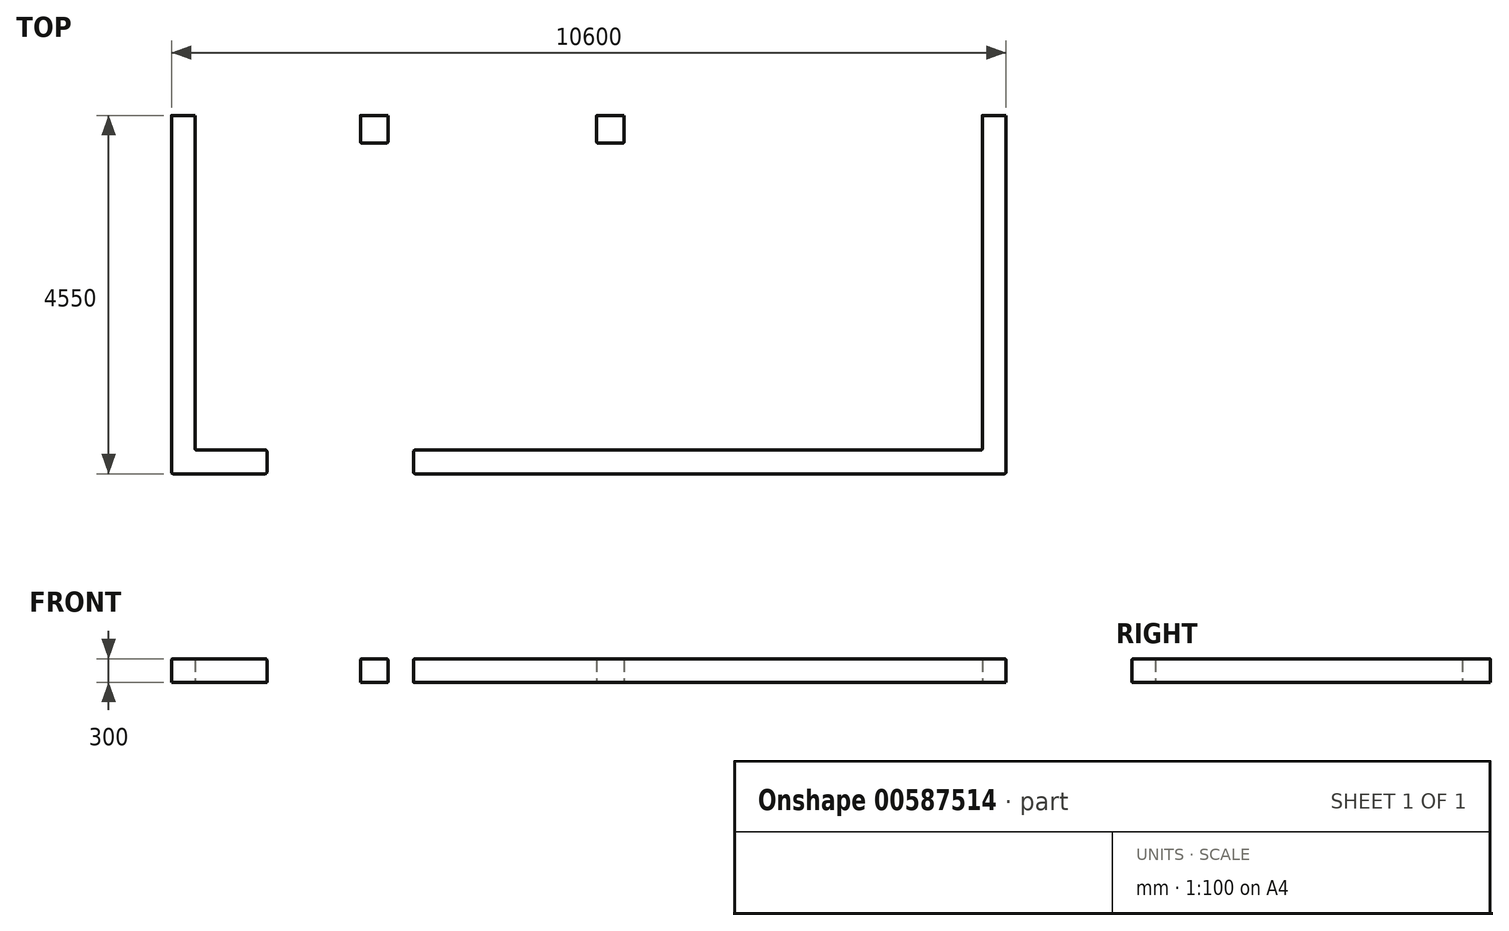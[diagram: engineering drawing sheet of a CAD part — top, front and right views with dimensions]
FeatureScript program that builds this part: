
annotation { "Feature Type Name" : "Feature", "Feature Type Description" : "" }
export const myFeature = defineFeature(function(context is Context, id is Id, definition is map)
    precondition{}
    {
        {
            var Q0;
            Q0=qCreatedBy(makeId("Top.planeOp"),FACE);
            var sketch = newSketch(context, id + "F0", { "sketchPlane" : qUnion([Q0])});
            skLineSegment(sketch, "E0.bottom", {"start": v(0, 0) * mm, "end": v(1211.59, 0) * mm});
            skLineSegment(sketch, "E0.top", {"start": v(0, 4550) * mm, "end": v(300, 4550) * mm});
            skLineSegment(sketch, "E0.left", {"start": v(0, 0) * mm, "end": v(0, 4550) * mm});
            skLineSegment(sketch, "E0.right", {"start": v(10600, 0) * mm, "end": v(10600, 4550) * mm});
            skLineSegment(sketch, "E1.1", {"start": v(300, 300) * mm, "end": v(300, 4550) * mm});
            skLineSegment(sketch, "E1.2", {"start": v(300, 300) * mm, "end": v(1211.59, 300) * mm});
            skLineSegment(sketch, "E1.3", {"start": v(10300, 300) * mm, "end": v(10300, 4550) * mm});
            skLineSegment(sketch, "E2.left", {"start": v(1211.59, 300) * mm, "end": v(1211.59, 0) * mm});
            skLineSegment(sketch, "E2.right", {"start": v(3074.35, 300) * mm, "end": v(3074.35, 0) * mm});
            skLineSegment(sketch, "E3.trimOffspring", {"start": v(3074.35, 300) * mm, "end": v(10300, 300) * mm});
            skLineSegment(sketch, "E4.trimOffspring", {"start": v(3074.35, 0) * mm, "end": v(10600, 0) * mm});
            skLineSegment(sketch, "E5.trimOffspring", {"start": v(10300, 4550) * mm, "end": v(10600, 4550) * mm});
            skLineSegment(sketch, "E6.bottom", {"start": v(2400, 4550) * mm, "end": v(2750, 4550) * mm});
            skLineSegment(sketch, "E6.top", {"start": v(2400, 4200) * mm, "end": v(2750, 4200) * mm});
            skLineSegment(sketch, "E6.left", {"start": v(2400, 4550) * mm, "end": v(2400, 4200) * mm});
            skLineSegment(sketch, "E6.right", {"start": v(2750, 4550) * mm, "end": v(2750, 4200) * mm});
            skLineSegment(sketch, "E7.bottom", {"start": v(5400, 4550) * mm, "end": v(5750, 4550) * mm});
            skLineSegment(sketch, "E7.top", {"start": v(5400, 4200) * mm, "end": v(5750, 4200) * mm});
            skLineSegment(sketch, "E7.left", {"start": v(5400, 4550) * mm, "end": v(5400, 4200) * mm});
            skLineSegment(sketch, "E7.right", {"start": v(5750, 4550) * mm, "end": v(5750, 4200) * mm});
            skSolve(sketch);
        }
        {
            var Q0;
            Q0 = qSketchRegion(id + "F0", true);
            extrude(context, id + "F1", {"entities" : qUnion([Q0]), "depth" : 300 * mm, "offsetDistance" : 25 * mm});
        }
        {
            var Q0;
            Q0=makeQuery(id+"F1.opExtrude","CAP_EDGE",EDGE,{"disambiguationData":[OSD([sQuery(id+"F0.wireOp",EDGE,"E1.1")])],"isStart":false});
            var Q1;
            Q1=makeQuery(id+"F1.opExtrude","CAP_EDGE",EDGE,{"disambiguationData":[OSD([sQuery(id+"F0.wireOp",EDGE,"E0.left")])],"isStart":false});
            var Q2;
            Q2=makeQuery(id+"F1.opExtrude","CAP_EDGE",EDGE,{"disambiguationData":[OSD([sQuery(id+"F0.wireOp",EDGE,"E1.2")])],"isStart":false});
            var Q3;
            Q3=makeQuery(id+"F1.opExtrude","CAP_EDGE",EDGE,{"disambiguationData":[OSD([sQuery(id+"F0.wireOp",EDGE,"E0.bottom")])],"isStart":false});
            var Q4;
            Q4=makeQuery(id+"F1.opExtrude","SWEPT_EDGE",EDGE,{"disambiguationData":[OSD([sQuery(id+"F0.wireOp",EDGE,"E0.bottom"),sQuery(id+"F0.wireOp",EDGE,"E2.left")])]});
            var Q5;
            Q5=makeQuery(id+"F1.opExtrude","CAP_EDGE",EDGE,{"disambiguationData":[OSD([sQuery(id+"F0.wireOp",EDGE,"E2.left")])],"isStart":false});
            var Q6;
            Q6=makeQuery(id+"F1.opExtrude","SWEPT_EDGE",EDGE,{"disambiguationData":[OSD([sQuery(id+"F0.wireOp",EDGE,"E1.2"),sQuery(id+"F0.wireOp",EDGE,"E2.left")])]});
            var Q7;
            Q7=makeQuery(id+"F1.opExtrude","SWEPT_EDGE",EDGE,{"disambiguationData":[OSD([sQuery(id+"F0.wireOp",EDGE,"E2.right"),sQuery(id+"F0.wireOp",EDGE,"E4.trimOffspring")])]});
            var Q8;
            Q8=makeQuery(id+"F1.opExtrude","CAP_EDGE",EDGE,{"disambiguationData":[OSD([sQuery(id+"F0.wireOp",EDGE,"E2.right")])],"isStart":false});
            var Q9;
            Q9=makeQuery(id+"F1.opExtrude","CAP_EDGE",EDGE,{"disambiguationData":[OSD([sQuery(id+"F0.wireOp",EDGE,"E3.trimOffspring")])],"isStart":false});
            var Q10;
            Q10=makeQuery(id+"F1.opExtrude","CAP_EDGE",EDGE,{"disambiguationData":[OSD([sQuery(id+"F0.wireOp",EDGE,"E4.trimOffspring")])],"isStart":false});
            var Q11;
            Q11=makeQuery(id+"F1.opExtrude","SWEPT_EDGE",EDGE,{"disambiguationData":[OSD([sQuery(id+"F0.wireOp",EDGE,"E2.right"),sQuery(id+"F0.wireOp",EDGE,"E3.trimOffspring")])]});
            var Q12;
            Q12=makeQuery(id+"F1.opExtrude","CAP_EDGE",EDGE,{"disambiguationData":[OSD([sQuery(id+"F0.wireOp",EDGE,"E1.3")])],"isStart":false});
            var Q13;
            Q13=makeQuery(id+"F1.opExtrude","CAP_EDGE",EDGE,{"disambiguationData":[OSD([sQuery(id+"F0.wireOp",EDGE,"E0.right")])],"isStart":false});
            var Q14;
            Q14=makeQuery(id+"F1.opExtrude","SWEPT_FACE",FACE,{"disambiguationData":[OSD([sQuery(id+"F0.wireOp",EDGE,"E4.trimOffspring")])]});
            var Q15;
            Q15=makeQuery(id+"F1.opExtrude","SWEPT_EDGE",EDGE,{"disambiguationData":[OSD([sQuery(id+"F0.wireOp",EDGE,"E0.bottom"),sQuery(id+"F0.wireOp",EDGE,"E0.left")])]});
            var Q16;
            Q16=makeQuery(id+"F1.opExtrude","SWEPT_EDGE",EDGE,{"disambiguationData":[OSD([sQuery(id+"F0.wireOp",EDGE,"E1.1"),sQuery(id+"F0.wireOp",EDGE,"E1.2")])]});
            var Q17;
            Q17=makeQuery(id+"F1.opExtrude","SWEPT_EDGE",EDGE,{"disambiguationData":[OSD([sQuery(id+"F0.wireOp",EDGE,"E1.3"),sQuery(id+"F0.wireOp",EDGE,"E3.trimOffspring")])]});
            var Q18;
            Q18=makeQuery(id+"F1.opExtrude","SWEPT_EDGE",EDGE,{"disambiguationData":[OSD([sQuery(id+"F0.wireOp",EDGE,"E6.top"),sQuery(id+"F0.wireOp",EDGE,"E6.left")])]});
            var Q19;
            Q19=makeQuery(id+"F1.opExtrude","CAP_EDGE",EDGE,{"disambiguationData":[OSD([sQuery(id+"F0.wireOp",EDGE,"E6.left")])],"isStart":false});
            var Q20;
            Q20=makeQuery(id+"F1.opExtrude","CAP_EDGE",EDGE,{"disambiguationData":[OSD([sQuery(id+"F0.wireOp",EDGE,"E6.top")])],"isStart":false});
            var Q21;
            Q21=makeQuery(id+"F1.opExtrude","SWEPT_EDGE",EDGE,{"disambiguationData":[OSD([sQuery(id+"F0.wireOp",EDGE,"E6.top"),sQuery(id+"F0.wireOp",EDGE,"E6.right")])]});
            var Q22;
            Q22=makeQuery(id+"F1.opExtrude","CAP_EDGE",EDGE,{"disambiguationData":[OSD([sQuery(id+"F0.wireOp",EDGE,"E6.right")])],"isStart":false});
            var Q23;
            Q23=makeQuery(id+"F1.opExtrude","SWEPT_EDGE",EDGE,{"disambiguationData":[OSD([sQuery(id+"F0.wireOp",EDGE,"E7.top"),sQuery(id+"F0.wireOp",EDGE,"E7.left")])]});
            var Q24;
            Q24=makeQuery(id+"F1.opExtrude","CAP_EDGE",EDGE,{"disambiguationData":[OSD([sQuery(id+"F0.wireOp",EDGE,"E7.top")])],"isStart":false});
            var Q25;
            Q25=makeQuery(id+"F1.opExtrude","CAP_EDGE",EDGE,{"disambiguationData":[OSD([sQuery(id+"F0.wireOp",EDGE,"E7.left")])],"isStart":false});
            var Q26;
            Q26=makeQuery(id+"F1.opExtrude","SWEPT_EDGE",EDGE,{"disambiguationData":[OSD([sQuery(id+"F0.wireOp",EDGE,"E7.top"),sQuery(id+"F0.wireOp",EDGE,"E7.right")])]});
            var Q27;
            Q27=makeQuery(id+"F1.opExtrude","CAP_EDGE",EDGE,{"disambiguationData":[OSD([sQuery(id+"F0.wireOp",EDGE,"E7.right")])],"isStart":false});
            fillet(context, id + "F2", {"entities" : qUnion([Q0, Q1, Q2, Q3, Q4, Q5, Q6, Q7, Q8, Q9, Q10, Q11, Q12, Q13, Q14, Q15, Q16, Q17, Q18, Q19, Q20, Q21, Q22, Q23, Q24, Q25, Q26, Q27]), "radius" : 20 * mm, "tangentPropagation" : true, "allowEdgeOverflow" : false});
        }
    });
